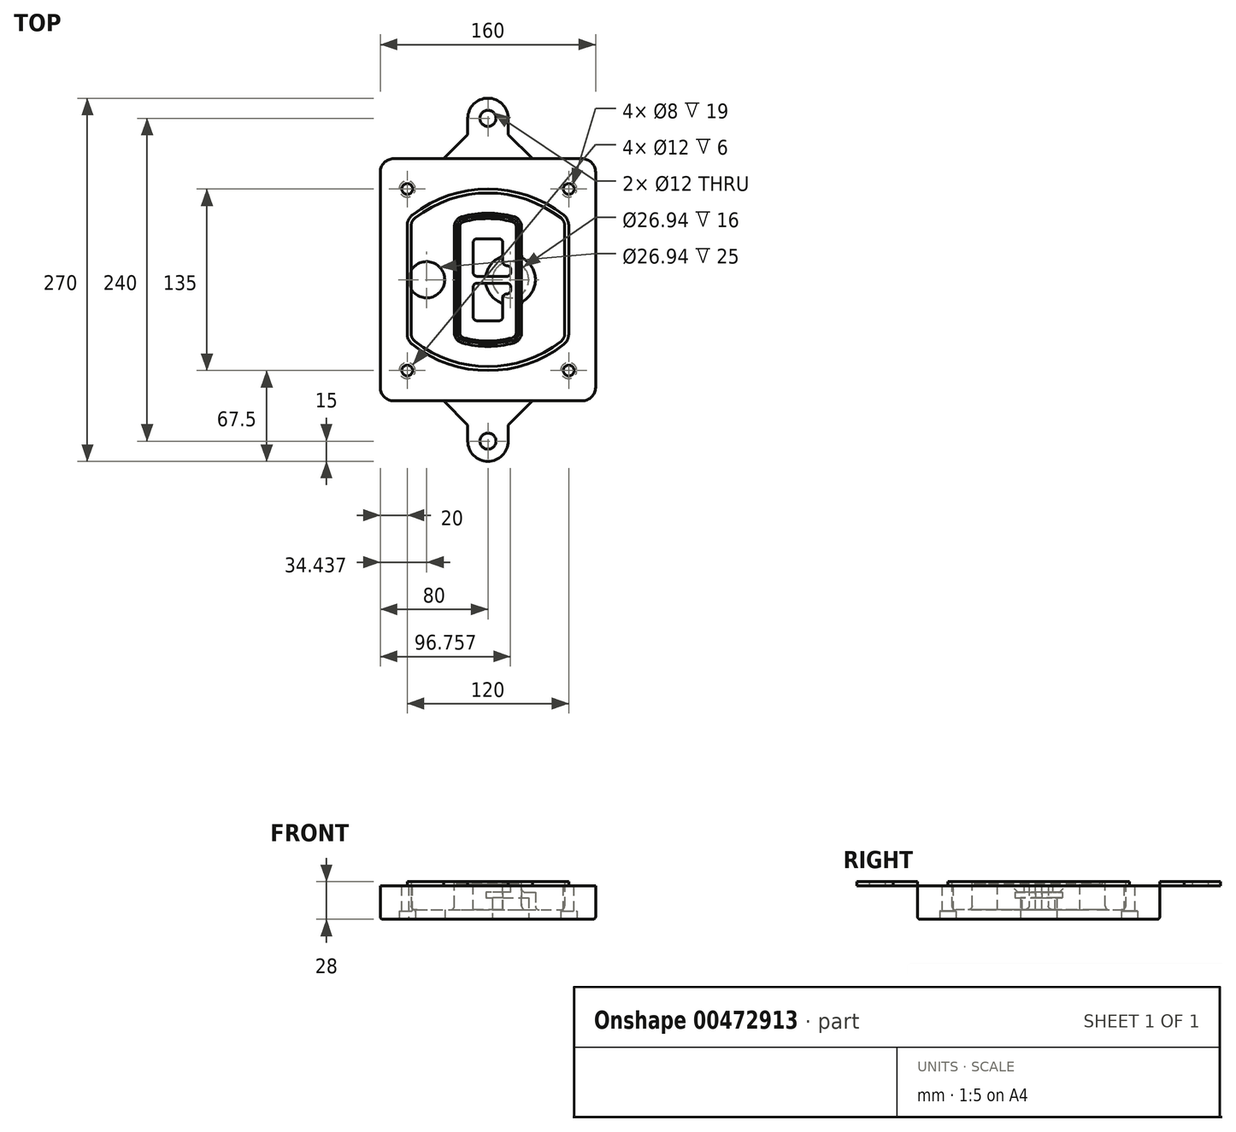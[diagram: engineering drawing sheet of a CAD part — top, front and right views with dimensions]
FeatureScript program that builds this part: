
annotation { "Feature Type Name" : "Feature", "Feature Type Description" : "" }
export const myFeature = defineFeature(function(context is Context, id is Id, definition is map)
    precondition{}
    {
        {
            var Q0;
            Q0=qCreatedBy(makeId("Top.planeOp"),FACE);
            var sketch = newSketch(context, id + "F0", { "sketchPlane" : qUnion([Q0])});
            skPoint(sketch, "E0.rect.middle", {"position": v(0, 0) * mm});
            skLineSegment(sketch, "E1.bottom", {"start": v(-70, -90) * mm, "end": v(70, -90) * mm});
            skLineSegment(sketch, "E1.top", {"start": v(-70, 90) * mm, "end": v(70, 90) * mm});
            skLineSegment(sketch, "E1.left", {"start": v(-80, -80) * mm, "end": v(-80, 80) * mm});
            skLineSegment(sketch, "E1.right", {"start": v(80, -80) * mm, "end": v(80, 80) * mm});
            skLineSegment(sketch, "E2", {"start": v(-80, 90) * mm, "end": v(80, -90) * mm, "construction": true});
            skLineSegment(sketch, "E3", {"start": v(80, 90) * mm, "end": v(-80, -90) * mm, "construction": true});
            skCircle(sketch, "E4", {"center": v(-60, 67.5) * mm, "radius": 4 * mm});
            skCircle(sketch, "E5", {"center": v(60, 67.5) * mm, "radius": 4 * mm});
            skCircle(sketch, "E6", {"center": v(60, -67.5) * mm, "radius": 4 * mm});
            skCircle(sketch, "E7", {"center": v(-60, -67.5) * mm, "radius": 4 * mm});
            skLineSegment(sketch, "E8", {"start": v(-60, 67.5) * mm, "end": v(60, 67.5) * mm, "construction": true});
            skLineSegment(sketch, "E9", {"start": v(60, 67.5) * mm, "end": v(60, -67.5) * mm, "construction": true});
            skLineSegment(sketch, "E10", {"start": v(60, -67.5) * mm, "end": v(-60, -67.5) * mm, "construction": true});
            skLineSegment(sketch, "E11", {"start": v(-60, -67.5) * mm, "end": v(-60, 67.5) * mm, "construction": true});
            skLineSegment(sketch, "E12", {"start": v(-60, 40.3) * mm, "end": v(-60, -40.3) * mm});
            skLineSegment(sketch, "E13", {"start": v(60, 40.3) * mm, "end": v(60, -40.3) * mm});
            skArc(sketch, "E14", {"start": v(56.15, 48.18) * mm, "mid": v(0, 67.5) * mm, "end": v(-56.15, 48.18) * mm});
            skArc(sketch, "E15", {"start": v(-56.15, -48.18) * mm, "mid": v(0, -67.5) * mm, "end": v(56.15, -48.18) * mm});
            skLineSegment(sketch, "E16", {"start": v(-60, 0) * mm, "end": v(60, 0) * mm, "construction": true});
            skPoint(sketch, "E17.visualSharp", {"position": v(-60, -45) * mm});
            skArc(sketch, "E17.filletArc", {"start": v(-60, -40.3) * mm, "mid": v(-58.99, -44.68) * mm, "end": v(-56.15, -48.18) * mm});
            skPoint(sketch, "E18.visualSharp", {"position": v(-60, 45) * mm});
            skArc(sketch, "E18.filletArc", {"start": v(-56.15, 48.18) * mm, "mid": v(-58.99, 44.68) * mm, "end": v(-60, 40.3) * mm});
            skPoint(sketch, "E19.visualSharp", {"position": v(60, 45) * mm});
            skArc(sketch, "E19.filletArc", {"start": v(60, 40.3) * mm, "mid": v(58.99, 44.68) * mm, "end": v(56.15, 48.18) * mm});
            skPoint(sketch, "E20.visualSharp", {"position": v(60, -45) * mm});
            skArc(sketch, "E20.filletArc", {"start": v(56.15, -48.18) * mm, "mid": v(58.99, -44.68) * mm, "end": v(60, -40.3) * mm});
            skPoint(sketch, "E21.visualSharp", {"position": v(-80, 90) * mm});
            skArc(sketch, "E21.filletArc", {"start": v(-70, 90) * mm, "mid": v(-77.07, 87.07) * mm, "end": v(-80, 80) * mm});
            skPoint(sketch, "E22.visualSharp", {"position": v(80, 90) * mm});
            skArc(sketch, "E22.filletArc", {"start": v(80, 80) * mm, "mid": v(77.07, 87.07) * mm, "end": v(70, 90) * mm});
            skPoint(sketch, "E23.visualSharp", {"position": v(80, -90) * mm});
            skArc(sketch, "E23.filletArc", {"start": v(70, -90) * mm, "mid": v(77.07, -87.07) * mm, "end": v(80, -80) * mm});
            skPoint(sketch, "E24.visualSharp", {"position": v(-80, -90) * mm});
            skArc(sketch, "E24.filletArc", {"start": v(-80, -80) * mm, "mid": v(-77.07, -87.07) * mm, "end": v(-70, -90) * mm});
            skArc(sketch, "E25.0", {"start": v(57, 40.3) * mm, "mid": v(56.3, 43.36) * mm, "end": v(54.3, 45.81) * mm});
            skLineSegment(sketch, "E25.1", {"start": v(57, 40.3) * mm, "end": v(57, -40.3) * mm});
            skArc(sketch, "E25.2", {"start": v(54.3, -45.81) * mm, "mid": v(56.3, -43.36) * mm, "end": v(57, -40.3) * mm});
            skArc(sketch, "E25.3", {"start": v(-54.3, -45.81) * mm, "mid": v(0, -64.5) * mm, "end": v(54.3, -45.81) * mm});
            skArc(sketch, "E25.4", {"start": v(-57, -40.3) * mm, "mid": v(-56.3, -43.36) * mm, "end": v(-54.3, -45.81) * mm});
            skArc(sketch, "E25.5", {"start": v(54.3, 45.81) * mm, "mid": v(0, 64.5) * mm, "end": v(-54.3, 45.81) * mm});
            skLineSegment(sketch, "E25.6", {"start": v(-57, 40.3) * mm, "end": v(-57, -40.3) * mm});
            skArc(sketch, "E25.7", {"start": v(-54.3, 45.81) * mm, "mid": v(-56.3, 43.36) * mm, "end": v(-57, 40.3) * mm});
            skArc(sketch, "E26.0", {"start": v(-58.62, 51.33) * mm, "mid": v(-62.58, 46.43) * mm, "end": v(-64, 40.3) * mm});
            skArc(sketch, "E26.1", {"start": v(58.62, 51.33) * mm, "mid": v(0, 71.5) * mm, "end": v(-58.62, 51.33) * mm});
            skArc(sketch, "E26.2", {"start": v(64, 40.3) * mm, "mid": v(62.58, 46.43) * mm, "end": v(58.62, 51.33) * mm});
            skLineSegment(sketch, "E26.3", {"start": v(64, 40.3) * mm, "end": v(64, -40.3) * mm});
            skArc(sketch, "E26.4", {"start": v(58.62, -51.33) * mm, "mid": v(62.58, -46.43) * mm, "end": v(64, -40.3) * mm});
            skLineSegment(sketch, "E26.5", {"start": v(-64, 40.3) * mm, "end": v(-64, -40.3) * mm});
            skArc(sketch, "E26.6", {"start": v(-58.62, -51.33) * mm, "mid": v(0, -71.5) * mm, "end": v(58.62, -51.33) * mm});
            skArc(sketch, "E26.7", {"start": v(-64, -40.3) * mm, "mid": v(-62.58, -46.43) * mm, "end": v(-58.62, -51.33) * mm});
            skSolve(sketch);
        }
        {
            var Q0;
            Q0=makeQuery(id+"F0.imprint","IMPRINT",FACE,{"disambiguationData":[TD([[makeQuery(id+"F0.imprint","IMPRINT",EDGE,{"derivedFrom":sQuery(id+"F0.wireOp",EDGE,"E1.bottom")}),1.0]])]});
            var Q1;
            Q1=makeQuery(id+"F0.imprint","IMPRINT",FACE,{"disambiguationData":[TD([[makeQuery(id+"F0.imprint","IMPRINT",EDGE,{"derivedFrom":sQuery(id+"F0.wireOp",EDGE,"E12")}),1.0]])]});
            var Q2;
            Q2=makeQuery(id+"F0.imprint","IMPRINT",FACE,{"disambiguationData":[TD([[makeQuery(id+"F0.imprint","IMPRINT",EDGE,{"derivedFrom":sQuery(id+"F0.wireOp",EDGE,"E25.0")}),1.0]])]});
            var Q3;
            Q3=makeQuery(id+"F0.imprint","IMPRINT",FACE,{"disambiguationData":[TD([[makeQuery(id+"F0.imprint","IMPRINT",EDGE,{"derivedFrom":sQuery(id+"F0.wireOp",EDGE,"E12")}),-1.0]])]});
            extrude(context, id + "F1", {"entities" : qUnion([Q0, Q1, Q2, Q3]), "oppositeDirection" : true, "depth" : 25 * mm});
        }
        {
            var Q0;
            Q0=makeQuery(id+"F0.imprint","IMPRINT",FACE,{"disambiguationData":[TD([[makeQuery(id+"F0.imprint","IMPRINT",EDGE,{"derivedFrom":sQuery(id+"F0.wireOp",EDGE,"E12")}),1.0]])]});
            extrude(context, id + "F2", {"entities" : qUnion([Q0]), "operationType" : NewBodyOperationType.ADD, "depth" : 3 * mm});
        }
        {
            var Q0;
            Q0=makeQuery(id+"F0.imprint","IMPRINT",FACE,{"disambiguationData":[TD([[makeQuery(id+"F0.imprint","IMPRINT",EDGE,{"derivedFrom":sQuery(id+"F0.wireOp",EDGE,"E25.0")}),1.0]])]});
            extrude(context, id + "F3", {"entities" : qUnion([Q0]), "operationType" : NewBodyOperationType.REMOVE, "oppositeDirection" : true, "depth" : 18 * mm});
        }
        {
            var Q0;
            Q0=makeQuery(id+"F2.opExtrude","CAP_FACE",FACE,{"disambiguationData":[OSD([sQuery(id+"F0.wireOp",EDGE,"E12"),sQuery(id+"F0.wireOp",EDGE,"E13"),sQuery(id+"F0.wireOp",EDGE,"E14"),sQuery(id+"F0.wireOp",EDGE,"E15"),sQuery(id+"F0.wireOp",EDGE,"E17.filletArc"),sQuery(id+"F0.wireOp",EDGE,"E18.filletArc"),sQuery(id+"F0.wireOp",EDGE,"E19.filletArc"),sQuery(id+"F0.wireOp",EDGE,"E20.filletArc"),sQuery(id+"F0.wireOp",EDGE,"E25.0"),sQuery(id+"F0.wireOp",EDGE,"E25.1"),sQuery(id+"F0.wireOp",EDGE,"E25.2"),sQuery(id+"F0.wireOp",EDGE,"E25.3"),sQuery(id+"F0.wireOp",EDGE,"E25.4"),sQuery(id+"F0.wireOp",EDGE,"E25.5"),sQuery(id+"F0.wireOp",EDGE,"E25.6"),sQuery(id+"F0.wireOp",EDGE,"E25.7")])],"isStart":false});
            var sketch = newSketch(context, id + "F4", { "sketchPlane" : qUnion([Q0])});
            skArc(sketch, "E27.0", {"start": v(-19.08, -46.97) * mm, "mid": v(0, -49.5) * mm, "end": v(19.08, -46.97) * mm});
            skArc(sketch, "E28.0", {"start": v(19.08, 46.97) * mm, "mid": v(0, 49.5) * mm, "end": v(-19.08, 46.97) * mm});
            skLineSegment(sketch, "E29", {"start": v(-25, 39.25) * mm, "end": v(-25, -39.25) * mm});
            skLineSegment(sketch, "E30", {"start": v(25, 39.25) * mm, "end": v(25, -39.25) * mm});
            skLineSegment(sketch, "E31", {"start": v(-25, 45.1) * mm, "end": v(25, 45.1) * mm, "construction": true});
            skLineSegment(sketch, "E32", {"start": v(-25, -45.1) * mm, "end": v(25, -45.1) * mm, "construction": true});
            skPoint(sketch, "E33.visualSharp", {"position": v(-25, 45.1) * mm});
            skArc(sketch, "E33.filletArc", {"start": v(-19.08, 46.97) * mm, "mid": v(-23.35, 44.11) * mm, "end": v(-25, 39.25) * mm});
            skPoint(sketch, "E34.visualSharp", {"position": v(25, 45.1) * mm});
            skArc(sketch, "E34.filletArc", {"start": v(25, 39.25) * mm, "mid": v(23.35, 44.11) * mm, "end": v(19.08, 46.97) * mm});
            skPoint(sketch, "E35.visualSharp", {"position": v(25, -45.1) * mm});
            skArc(sketch, "E35.filletArc", {"start": v(19.08, -46.97) * mm, "mid": v(23.35, -44.11) * mm, "end": v(25, -39.25) * mm});
            skPoint(sketch, "E36.visualSharp", {"position": v(-25, -45.1) * mm});
            skArc(sketch, "E36.filletArc", {"start": v(-25, -39.25) * mm, "mid": v(-23.35, -44.11) * mm, "end": v(-19.08, -46.97) * mm});
            skArc(sketch, "E37.0", {"start": v(54.3, 45.81) * mm, "mid": v(0, 64.5) * mm, "end": v(-54.3, 45.81) * mm});
            skArc(sketch, "E37.1", {"start": v(-54.3, 45.81) * mm, "mid": v(-56.3, 43.36) * mm, "end": v(-57, 40.3) * mm});
            skLineSegment(sketch, "E37.2", {"start": v(-57, 40.3) * mm, "end": v(-57, -40.3) * mm});
            skArc(sketch, "E37.3", {"start": v(-57, -40.3) * mm, "mid": v(-56.3, -43.36) * mm, "end": v(-54.3, -45.81) * mm});
            skArc(sketch, "E37.4", {"start": v(-54.3, -45.81) * mm, "mid": v(0, -64.5) * mm, "end": v(54.3, -45.81) * mm});
            skArc(sketch, "E37.5", {"start": v(54.3, -45.81) * mm, "mid": v(56.3, -43.36) * mm, "end": v(57, -40.3) * mm});
            skLineSegment(sketch, "E37.6", {"start": v(57, 40.3) * mm, "end": v(57, -40.3) * mm});
            skArc(sketch, "E37.7", {"start": v(57, 40.3) * mm, "mid": v(56.3, 43.36) * mm, "end": v(54.3, 45.81) * mm});
            skLineSegment(sketch, "E38.0", {"start": v(23, 39.25) * mm, "end": v(23, -39.25) * mm});
            skArc(sketch, "E38.1", {"start": v(18.56, -45.04) * mm, "mid": v(21.76, -42.9) * mm, "end": v(23, -39.25) * mm});
            skArc(sketch, "E38.2", {"start": v(-18.56, -45.04) * mm, "mid": v(0, -47.5) * mm, "end": v(18.56, -45.04) * mm});
            skArc(sketch, "E38.3", {"start": v(-23, -39.25) * mm, "mid": v(-21.76, -42.9) * mm, "end": v(-18.56, -45.04) * mm});
            skLineSegment(sketch, "E38.4", {"start": v(-23, 39.25) * mm, "end": v(-23, -39.25) * mm});
            skArc(sketch, "E38.5", {"start": v(23, 39.25) * mm, "mid": v(21.76, 42.9) * mm, "end": v(18.56, 45.04) * mm});
            skArc(sketch, "E38.6", {"start": v(-18.56, 45.04) * mm, "mid": v(-21.76, 42.9) * mm, "end": v(-23, 39.25) * mm});
            skArc(sketch, "E38.7", {"start": v(18.56, 45.04) * mm, "mid": v(0, 47.5) * mm, "end": v(-18.56, 45.04) * mm});
            skArc(sketch, "E39.0", {"start": v(21, 39.25) * mm, "mid": v(20.18, 41.68) * mm, "end": v(18.04, 43.1) * mm});
            skLineSegment(sketch, "E39.1", {"start": v(21, 39.25) * mm, "end": v(21, -39.25) * mm});
            skArc(sketch, "E39.2", {"start": v(18.04, -43.1) * mm, "mid": v(20.18, -41.68) * mm, "end": v(21, -39.25) * mm});
            skArc(sketch, "E39.3", {"start": v(-18.04, -43.1) * mm, "mid": v(0, -45.5) * mm, "end": v(18.04, -43.1) * mm});
            skArc(sketch, "E39.4", {"start": v(-21, -39.25) * mm, "mid": v(-20.18, -41.68) * mm, "end": v(-18.04, -43.1) * mm});
            skArc(sketch, "E39.5", {"start": v(18.04, 43.1) * mm, "mid": v(0, 45.5) * mm, "end": v(-18.04, 43.1) * mm});
            skLineSegment(sketch, "E39.6", {"start": v(-21, 39.25) * mm, "end": v(-21, -39.25) * mm});
            skArc(sketch, "E39.7", {"start": v(-18.04, 43.1) * mm, "mid": v(-20.18, 41.68) * mm, "end": v(-21, 39.25) * mm});
            skLineSegment(sketch, "E40", {"start": v(-25, 0) * mm, "end": v(25, 0) * mm, "construction": true});
            skLineSegment(sketch, "E41", {"start": v(-11, 5.5) * mm, "end": v(-11, 27.5) * mm});
            skLineSegment(sketch, "E42", {"start": v(-8, 30.5) * mm, "end": v(8, 30.5) * mm});
            skLineSegment(sketch, "E43", {"start": v(11, 27.5) * mm, "end": v(11, 13.5) * mm});
            skLineSegment(sketch, "E44", {"start": v(14, 10.5) * mm, "end": v(14, 10.5) * mm});
            skLineSegment(sketch, "E45", {"start": v(17, 7.5) * mm, "end": v(17, 5.5) * mm});
            skLineSegment(sketch, "E46", {"start": v(14, 2.5) * mm, "end": v(-8, 2.5) * mm});
            skPoint(sketch, "E47.visualSharp", {"position": v(-11, 30.5) * mm});
            skArc(sketch, "E47.filletArc", {"start": v(-8, 30.5) * mm, "mid": v(-10.12, 29.62) * mm, "end": v(-11, 27.5) * mm});
            skPoint(sketch, "E48.visualSharp", {"position": v(11, 30.5) * mm});
            skArc(sketch, "E48.filletArc", {"start": v(11, 27.5) * mm, "mid": v(10.12, 29.62) * mm, "end": v(8, 30.5) * mm});
            skPoint(sketch, "E49.visualSharp", {"position": v(11, 10.5) * mm});
            skArc(sketch, "E49.filletArc", {"start": v(11, 13.5) * mm, "mid": v(11.88, 11.38) * mm, "end": v(14, 10.5) * mm});
            skPoint(sketch, "E50.visualSharp", {"position": v(17, 10.5) * mm});
            skArc(sketch, "E50.filletArc", {"start": v(17, 7.5) * mm, "mid": v(16.12, 9.62) * mm, "end": v(14, 10.5) * mm});
            skPoint(sketch, "E51.visualSharp", {"position": v(17, 2.5) * mm});
            skArc(sketch, "E51.filletArc", {"start": v(14, 2.5) * mm, "mid": v(16.12, 3.38) * mm, "end": v(17, 5.5) * mm});
            skPoint(sketch, "E52.visualSharp", {"position": v(-11, 2.5) * mm});
            skArc(sketch, "E52.filletArc", {"start": v(-11, 5.5) * mm, "mid": v(-10.12, 3.38) * mm, "end": v(-8, 2.5) * mm});
            skLineSegment(sketch, "E53.0.MirrorCS", {"start": v(14, -2.5) * mm, "end": v(-8, -2.5) * mm});
            skArc(sketch, "E54.0.MirrorCS", {"start": v(-11, -5.5) * mm, "mid": v(-10.12, -3.38) * mm, "end": v(-8, -2.5) * mm});
            skLineSegment(sketch, "E55.0.MirrorCS", {"start": v(-11, -5.5) * mm, "end": v(-11, -27.5) * mm});
            skArc(sketch, "E56.0.MirrorCS", {"start": v(-8, -30.5) * mm, "mid": v(-10.12, -29.62) * mm, "end": v(-11, -27.5) * mm});
            skLineSegment(sketch, "E57.0.MirrorCS", {"start": v(-8, -30.5) * mm, "end": v(8, -30.5) * mm});
            skArc(sketch, "E58.0.MirrorCS", {"start": v(11, -27.5) * mm, "mid": v(10.12, -29.62) * mm, "end": v(8, -30.5) * mm});
            skLineSegment(sketch, "E59.0.MirrorCS", {"start": v(11, -27.5) * mm, "end": v(11, -13.5) * mm});
            skArc(sketch, "E60.0.MirrorCS", {"start": v(11, -13.5) * mm, "mid": v(11.88, -11.38) * mm, "end": v(14, -10.5) * mm});
            skArc(sketch, "E61.0.MirrorCS", {"start": v(17, -7.5) * mm, "mid": v(16.12, -9.62) * mm, "end": v(14, -10.5) * mm});
            skLineSegment(sketch, "E62.0.MirrorCS", {"start": v(17, -7.5) * mm, "end": v(17, -5.5) * mm});
            skArc(sketch, "E63.0.MirrorCS", {"start": v(14, -2.5) * mm, "mid": v(16.12, -3.38) * mm, "end": v(17, -5.5) * mm});
            skSolve(sketch);
        }
        {
            var Q0;
            Q0=makeQuery(id+"F4.imprint","IMPRINT",FACE,{"disambiguationData":[TD([[makeQuery(id+"F4.imprint","IMPRINT",EDGE,{"derivedFrom":sQuery(id+"F4.wireOp",EDGE,"E27.0")}),1.0]])]});
            var Q1;
            Q1=makeQuery(id+"F4.imprint","IMPRINT",FACE,{"disambiguationData":[TD([[makeQuery(id+"F4.imprint","IMPRINT",EDGE,{"derivedFrom":sQuery(id+"F4.wireOp",EDGE,"E38.0")}),-1.0]])]});
            var Q2;
            Q2=makeQuery(id+"F4.imprint","IMPRINT",FACE,{"disambiguationData":[TD([[makeQuery(id+"F4.imprint","IMPRINT",EDGE,{"derivedFrom":sQuery(id+"F4.wireOp",EDGE,"E39.0")}),1.0]])]});
            extrude(context, id + "F5", {"entities" : qUnion([Q0, Q1, Q2]), "operationType" : NewBodyOperationType.ADD, "endBound" : BoundingType.UP_TO_NEXT, "oppositeDirection" : true, "depth" : 25 * mm});
        }
        {
            var Q0;
            Q0=makeQuery(id+"F4.imprint","IMPRINT",FACE,{"disambiguationData":[TD([[makeQuery(id+"F4.imprint","IMPRINT",EDGE,{"derivedFrom":sQuery(id+"F4.wireOp",EDGE,"E38.0")}),-1.0]])]});
            extrude(context, id + "F6", {"entities" : qUnion([Q0]), "operationType" : NewBodyOperationType.REMOVE, "oppositeDirection" : true, "depth" : 2 * mm});
        }
        {
            var Q0;
            Q0=makeQuery(id+"F1.opExtrude","CAP_FACE",FACE,{"disambiguationData":[OSD([sQuery(id+"F0.wireOp",EDGE,"E1.bottom"),sQuery(id+"F0.wireOp",EDGE,"E1.top"),sQuery(id+"F0.wireOp",EDGE,"E1.left"),sQuery(id+"F0.wireOp",EDGE,"E1.right"),sQuery(id+"F0.wireOp",EDGE,"E4"),sQuery(id+"F0.wireOp",EDGE,"E5"),sQuery(id+"F0.wireOp",EDGE,"E6"),sQuery(id+"F0.wireOp",EDGE,"E7"),sQuery(id+"F0.wireOp",EDGE,"E21.filletArc"),sQuery(id+"F0.wireOp",EDGE,"E22.filletArc"),sQuery(id+"F0.wireOp",EDGE,"E23.filletArc"),sQuery(id+"F0.wireOp",EDGE,"E24.filletArc")])],"isStart":false});
            var sketch = newSketch(context, id + "F7", { "sketchPlane" : qUnion([Q0])});
            skCircle(sketch, "E64", {"center": v(16.76, 0) * mm, "radius": 13.47 * mm});
            skCircle(sketch, "E65", {"center": v(-45.56, 0) * mm, "radius": 13.47 * mm});
            skLineSegment(sketch, "E66", {"start": v(80, 0) * mm, "end": v(-80, 0) * mm});
            skCircle(sketch, "E67", {"center": v(16.76, 0) * mm, "radius": 18.47 * mm});
            skCircle(sketch, "E68", {"center": v(60, -67.5) * mm, "radius": 6 * mm});
            skCircle(sketch, "E69", {"center": v(-60, -67.5) * mm, "radius": 6 * mm});
            skCircle(sketch, "E70", {"center": v(-60, 67.5) * mm, "radius": 6 * mm});
            skCircle(sketch, "E71", {"center": v(60, 67.5) * mm, "radius": 6 * mm});
            skSolve(sketch);
        }
        {
            var Q0;
            {var subQ1=sQuery(id+"F7.wireOp",EDGE,"E66");var subQ4=sQuery(id+"F7.wireOp",EDGE,"E64");var subQ6=makeQuery(id+"F7.imprint","INTERSECT",VERTEX,{"disambiguationData":[OD(0.0)],"derivedFrom":[subQ4,subQ1]});Q0=makeQuery(id+"F7.imprint","IMPRINT",FACE,{"disambiguationData":[TD([[makeQuery(id+"F7.imprint","IMPRINT",EDGE,{"disambiguationData":[TD([[subQ6,-1.0]])],"derivedFrom":subQ4}),-1.0]])]});}
            var Q1;
            {var subQ0=sQuery(id+"F7.wireOp",EDGE,"E66");var subQ1=sQuery(id+"F7.wireOp",EDGE,"E64");var subQ3=makeQuery(id+"F7.imprint","INTERSECT",VERTEX,{"disambiguationData":[OD(0.0)],"derivedFrom":[subQ1,subQ0]});Q1=makeQuery(id+"F7.imprint","IMPRINT",FACE,{"disambiguationData":[TD([[makeQuery(id+"F7.imprint","IMPRINT",EDGE,{"disambiguationData":[TD([[subQ3,-1.0]])],"derivedFrom":subQ1}),1.0]])]});}
            var Q2;
            {var subQ0=sQuery(id+"F7.wireOp",EDGE,"E66");var subQ1=sQuery(id+"F7.wireOp",EDGE,"E64");var subQ3=makeQuery(id+"F7.imprint","INTERSECT",VERTEX,{"disambiguationData":[OD(0.0)],"derivedFrom":[subQ1,subQ0]});Q2=makeQuery(id+"F7.imprint","IMPRINT",FACE,{"disambiguationData":[TD([[makeQuery(id+"F7.imprint","IMPRINT",EDGE,{"disambiguationData":[TD([[subQ3,1.0]])],"derivedFrom":subQ1}),1.0]])]});}
            var Q3;
            {var subQ1=sQuery(id+"F7.wireOp",EDGE,"E66");var subQ4=sQuery(id+"F7.wireOp",EDGE,"E64");var subQ6=makeQuery(id+"F7.imprint","INTERSECT",VERTEX,{"disambiguationData":[OD(0.0)],"derivedFrom":[subQ4,subQ1]});Q3=makeQuery(id+"F7.imprint","IMPRINT",FACE,{"disambiguationData":[TD([[makeQuery(id+"F7.imprint","IMPRINT",EDGE,{"disambiguationData":[TD([[subQ6,1.0]])],"derivedFrom":subQ4}),-1.0]])]});}
            extrude(context, id + "F8", {"entities" : qUnion([Q0, Q1, Q2, Q3]), "operationType" : NewBodyOperationType.ADD, "oppositeDirection" : true, "depth" : 20 * mm});
        }
        {
            var Q0;
            {var subQ0=sQuery(id+"F7.wireOp",EDGE,"E66");var subQ1=sQuery(id+"F7.wireOp",EDGE,"E64");var subQ3=makeQuery(id+"F7.imprint","INTERSECT",VERTEX,{"disambiguationData":[OD(0.0)],"derivedFrom":[subQ1,subQ0]});Q0=makeQuery(id+"F7.imprint","IMPRINT",FACE,{"disambiguationData":[TD([[makeQuery(id+"F7.imprint","IMPRINT",EDGE,{"disambiguationData":[TD([[subQ3,-1.0]])],"derivedFrom":subQ1}),1.0]])]});}
            var Q1;
            {var subQ0=sQuery(id+"F7.wireOp",EDGE,"E66");var subQ1=sQuery(id+"F7.wireOp",EDGE,"E64");var subQ3=makeQuery(id+"F7.imprint","INTERSECT",VERTEX,{"disambiguationData":[OD(0.0)],"derivedFrom":[subQ1,subQ0]});Q1=makeQuery(id+"F7.imprint","IMPRINT",FACE,{"disambiguationData":[TD([[makeQuery(id+"F7.imprint","IMPRINT",EDGE,{"disambiguationData":[TD([[subQ3,1.0]])],"derivedFrom":subQ1}),1.0]])]});}
            extrude(context, id + "F9", {"entities" : qUnion([Q0, Q1]), "operationType" : NewBodyOperationType.REMOVE, "oppositeDirection" : true, "depth" : 16 * mm});
        }
        {
            var Q0;
            {var subQ0=sQuery(id+"F7.wireOp",EDGE,"E66");var subQ1=sQuery(id+"F7.wireOp",EDGE,"E65");var subQ3=makeQuery(id+"F7.imprint","INTERSECT",VERTEX,{"disambiguationData":[OD(0.0)],"derivedFrom":[subQ1,subQ0]});Q0=makeQuery(id+"F7.imprint","IMPRINT",FACE,{"disambiguationData":[TD([[makeQuery(id+"F7.imprint","IMPRINT",EDGE,{"disambiguationData":[TD([[subQ3,-1.0]])],"derivedFrom":subQ1}),1.0]])]});}
            var Q1;
            {var subQ0=sQuery(id+"F7.wireOp",EDGE,"E66");var subQ1=sQuery(id+"F7.wireOp",EDGE,"E65");var subQ3=makeQuery(id+"F7.imprint","INTERSECT",VERTEX,{"disambiguationData":[OD(0.0)],"derivedFrom":[subQ1,subQ0]});Q1=makeQuery(id+"F7.imprint","IMPRINT",FACE,{"disambiguationData":[TD([[makeQuery(id+"F7.imprint","IMPRINT",EDGE,{"disambiguationData":[TD([[subQ3,1.0]])],"derivedFrom":subQ1}),1.0]])]});}
            extrude(context, id + "F10", {"entities" : qUnion([Q0, Q1]), "operationType" : NewBodyOperationType.REMOVE, "oppositeDirection" : true, "depth" : 25 * mm});
        }
        {
            var Q0;
            Q0=makeQuery(id+"F7.imprint","IMPRINT",FACE,{"disambiguationData":[TD([[makeQuery(id+"F7.imprint","IMPRINT",EDGE,{"derivedFrom":sQuery(id+"F7.wireOp",EDGE,"E68")}),1.0]])]});
            var Q1;
            Q1=makeQuery(id+"F7.imprint","IMPRINT",FACE,{"disambiguationData":[TD([[makeQuery(id+"F7.imprint","IMPRINT",EDGE,{"derivedFrom":makeQuery(id+"F1.opExtrude","CAP_EDGE",EDGE,{"disambiguationData":[OSD([sQuery(id+"F0.wireOp",EDGE,"E5")])],"isStart":false})}),-1.0]])]});
            var Q2;
            Q2=makeQuery(id+"F7.imprint","IMPRINT",FACE,{"disambiguationData":[TD([[makeQuery(id+"F7.imprint","IMPRINT",EDGE,{"derivedFrom":sQuery(id+"F7.wireOp",EDGE,"E69")}),1.0]])]});
            var Q3;
            Q3=makeQuery(id+"F7.imprint","IMPRINT",FACE,{"disambiguationData":[TD([[makeQuery(id+"F7.imprint","IMPRINT",EDGE,{"derivedFrom":makeQuery(id+"F1.opExtrude","CAP_EDGE",EDGE,{"disambiguationData":[OSD([sQuery(id+"F0.wireOp",EDGE,"E4")])],"isStart":false})}),-1.0]])]});
            var Q4;
            Q4=makeQuery(id+"F7.imprint","IMPRINT",FACE,{"disambiguationData":[TD([[makeQuery(id+"F7.imprint","IMPRINT",EDGE,{"derivedFrom":sQuery(id+"F7.wireOp",EDGE,"E70")}),1.0]])]});
            var Q5;
            Q5=makeQuery(id+"F7.imprint","IMPRINT",FACE,{"disambiguationData":[TD([[makeQuery(id+"F7.imprint","IMPRINT",EDGE,{"derivedFrom":makeQuery(id+"F1.opExtrude","CAP_EDGE",EDGE,{"disambiguationData":[OSD([sQuery(id+"F0.wireOp",EDGE,"E7")])],"isStart":false})}),-1.0]])]});
            var Q6;
            Q6=makeQuery(id+"F7.imprint","IMPRINT",FACE,{"disambiguationData":[TD([[makeQuery(id+"F7.imprint","IMPRINT",EDGE,{"derivedFrom":sQuery(id+"F7.wireOp",EDGE,"E71")}),1.0]])]});
            var Q7;
            Q7=makeQuery(id+"F7.imprint","IMPRINT",FACE,{"disambiguationData":[TD([[makeQuery(id+"F7.imprint","IMPRINT",EDGE,{"derivedFrom":makeQuery(id+"F1.opExtrude","CAP_EDGE",EDGE,{"disambiguationData":[OSD([sQuery(id+"F0.wireOp",EDGE,"E6")])],"isStart":false})}),-1.0]])]});
            extrude(context, id + "F11", {"entities" : qUnion([Q0, Q1, Q2, Q3, Q4, Q5, Q6, Q7]), "operationType" : NewBodyOperationType.REMOVE, "oppositeDirection" : true, "depth" : 6 * mm});
        }
        {
            var Q0;
            Q0=makeQuery(id+"F9.boolean.opBoolean","COPY",FACE,{"derivedFrom":makeQuery(id+"F9.opExtrude","CAP_FACE",FACE,{"disambiguationData":[OSD([sQuery(id+"F7.wireOp",EDGE,"E64")])],"isStart":false})});
            var sketch = newSketch(context, id + "F12", { "sketchPlane" : qUnion([Q0])});
            skArc(sketch, "E72.0", {"start": v(11, 17.55) * mm, "mid": v(2.57, 11.82) * mm, "end": v(-1.54, 2.5) * mm});
            skArc(sketch, "E72.1", {"start": v(-1.54, -2.5) * mm, "mid": v(2.57, -11.82) * mm, "end": v(11, -17.55) * mm});
            skLineSegment(sketch, "E73", {"start": v(-1.54, -2.5) * mm, "end": v(14, -2.5) * mm});
            skLineSegment(sketch, "E74.0", {"start": v(14, 2.5) * mm, "end": v(-1.54, 2.5) * mm});
            skArc(sketch, "E74.1", {"start": v(14, 2.5) * mm, "mid": v(16.12, 3.38) * mm, "end": v(17, 5.5) * mm});
            skLineSegment(sketch, "E74.2", {"start": v(17, 7.5) * mm, "end": v(17, 5.5) * mm});
            skArc(sketch, "E74.3", {"start": v(17, 7.5) * mm, "mid": v(16.12, 9.62) * mm, "end": v(14, 10.5) * mm});
            skArc(sketch, "E74.4", {"start": v(11, 13.5) * mm, "mid": v(11.88, 11.38) * mm, "end": v(14, 10.5) * mm});
            skLineSegment(sketch, "E74.5", {"start": v(11, 17.55) * mm, "end": v(11, 13.5) * mm});
            skLineSegment(sketch, "E74.7", {"start": v(14, -2.5) * mm, "end": v(-1.54, -2.5) * mm});
            skArc(sketch, "E74.8", {"start": v(14, -2.5) * mm, "mid": v(16.12, -3.38) * mm, "end": v(17, -5.5) * mm});
            skLineSegment(sketch, "E74.9", {"start": v(17, -7.5) * mm, "end": v(17, -5.5) * mm});
            skArc(sketch, "E74.10", {"start": v(17, -7.5) * mm, "mid": v(16.12, -9.62) * mm, "end": v(14, -10.5) * mm});
            skArc(sketch, "E74.11", {"start": v(11, -13.5) * mm, "mid": v(11.88, -11.38) * mm, "end": v(14, -10.5) * mm});
            skLineSegment(sketch, "E74.12", {"start": v(11, -17.55) * mm, "end": v(11, -13.5) * mm});
            skPoint(sketch, "E75.orphan", {"position": v(11, -27.5) * mm});
            skPoint(sketch, "E76.orphan", {"position": v(-8, -2.5) * mm});
            skPoint(sketch, "E77.orphan", {"position": v(-8, 2.5) * mm});
            skPoint(sketch, "E78.orphan", {"position": v(11, 27.5) * mm});
            skSolve(sketch);
        }
        {
            var Q0;
            {var subQ7=sQuery(id+"F12.wireOp",EDGE,"E72.0");var subQ14=sQuery(id+"F12.wireOp",EDGE,"E72.1");var subQ16=sQuery(id+"F12.wireOp",EDGE,"E74.1");var subQ18=sQuery(id+"F12.wireOp",EDGE,"E74.8");Q0=qUnion([makeQuery(id+"F12.imprint","IMPRINT",FACE,{"disambiguationData":[TD([[makeQuery(id+"F12.imprint","IMPRINT",EDGE,{"derivedFrom":subQ7}),1.0]])]}),makeQuery(id+"F12.imprint","IMPRINT",FACE,{"disambiguationData":[TD([[makeQuery(id+"F12.imprint","IMPRINT",EDGE,{"derivedFrom":subQ14}),1.0]])]}),makeQuery(id+"F12.imprint","IMPRINT",FACE,{"disambiguationData":[TD([[makeQuery(id+"F12.imprint","IMPRINT",EDGE,{"derivedFrom":subQ16}),1.0]])]}),makeQuery(id+"F12.imprint","IMPRINT",FACE,{"disambiguationData":[TD([[makeQuery(id+"F12.imprint","IMPRINT",EDGE,{"derivedFrom":subQ18}),-1.0]])]})]);}
            var Q1;
            Q1=makeQuery(id+"F5.boolean.opBoolean","SPLIT",FACE,{"disambiguationData":[TD([makeQuery(id+"F5.opExtrude","SWEPT_FACE",FACE,{"disambiguationData":[OSD([sQuery(id+"F4.wireOp",EDGE,"E41")])]})])],"derivedFrom":makeQuery(id+"F3.boolean.opBoolean","COPY",FACE,{"derivedFrom":makeQuery(id+"F3.opExtrude","CAP_FACE",FACE,{"disambiguationData":[OSD([sQuery(id+"F0.wireOp",EDGE,"E25.0"),sQuery(id+"F0.wireOp",EDGE,"E25.1"),sQuery(id+"F0.wireOp",EDGE,"E25.2"),sQuery(id+"F0.wireOp",EDGE,"E25.3"),sQuery(id+"F0.wireOp",EDGE,"E25.4"),sQuery(id+"F0.wireOp",EDGE,"E25.5"),sQuery(id+"F0.wireOp",EDGE,"E25.6"),sQuery(id+"F0.wireOp",EDGE,"E25.7")])],"isStart":false})})});
            extrude(context, id + "F13", {"entities" : qUnion([Q0]), "operationType" : NewBodyOperationType.REMOVE, "endBound" : BoundingType.UP_TO_SURFACE, "endBoundEntityFace" : qUnion([Q1]), "depth" : 25 * mm});
        }
        {
            var Q0;
            Q0=makeQuery(id+"F3.boolean.opBoolean","COPY",EDGE,{"derivedFrom":makeQuery(id+"F3.opExtrude","CAP_EDGE",EDGE,{"disambiguationData":[OSD([sQuery(id+"F0.wireOp",EDGE,"E25.6")])],"isStart":false})});
            var Q1;
            Q1=makeQuery(id+"F8.boolean.opBoolean","INTERSECT",EDGE,{"derivedFrom":[makeQuery(id+"F5.opExtrude","SWEPT_FACE",FACE,{"disambiguationData":[OSD([sQuery(id+"F4.wireOp",EDGE,"E30")])]}),makeQuery(id+"F8.opExtrude","CAP_FACE",FACE,{"disambiguationData":[OSD([sQuery(id+"F7.wireOp",EDGE,"E67")])],"isStart":false})]});
            var Q2;
            Q2=makeQuery(id+"F8.boolean.opBoolean","INTERSECT",EDGE,{"disambiguationData":[OD(1.0)],"derivedFrom":[makeQuery(id+"F5.opExtrude","SWEPT_FACE",FACE,{"disambiguationData":[OSD([sQuery(id+"F4.wireOp",EDGE,"E30")])]}),makeQuery(id+"F8.opExtrude","SWEPT_FACE",FACE,{"disambiguationData":[OSD([sQuery(id+"F7.wireOp",EDGE,"E67")])]})]});
            var Q3;
            {var subQ0=sQuery(id+"F4.wireOp",EDGE,"E30");Q3=makeQuery(id+"F8.boolean.opBoolean","SPLIT",EDGE,{"disambiguationData":[TD([makeQuery(id+"F5.opExtrude","SWEPT_FACE",FACE,{"disambiguationData":[OSD([sQuery(id+"F4.wireOp",EDGE,"E35.filletArc")])]})])],"derivedFrom":makeQuery(id+"F5.opExtrude","CAP_EDGE",EDGE,{"disambiguationData":[OSD([subQ0])],"isStart":false})});}
            var Q4;
            {var subQ0=sQuery(id+"F0.wireOp",EDGE,"E25.7");var subQ1=sQuery(id+"F0.wireOp",EDGE,"E25.1");var subQ2=sQuery(id+"F0.wireOp",EDGE,"E25.6");var subQ3=sQuery(id+"F0.wireOp",EDGE,"E25.5");var subQ4=sQuery(id+"F0.wireOp",EDGE,"E25.4");var subQ5=sQuery(id+"F0.wireOp",EDGE,"E25.0");var subQ6=sQuery(id+"F0.wireOp",EDGE,"E25.2");var subQ7=sQuery(id+"F0.wireOp",EDGE,"E25.3");Q4=makeQuery(id+"F8.boolean.opBoolean","INTERSECT",EDGE,{"derivedFrom":[makeQuery(id+"F5.boolean.opBoolean","SPLIT",FACE,{"disambiguationData":[TD([makeQuery(id+"F2.opExtrude","SWEPT_FACE",FACE,{"disambiguationData":[OSD([subQ5])]})])],"derivedFrom":makeQuery(id+"F3.boolean.opBoolean","COPY",FACE,{"derivedFrom":makeQuery(id+"F3.opExtrude","CAP_FACE",FACE,{"disambiguationData":[OSD([subQ5,subQ1,subQ6,subQ7,subQ4,subQ3,subQ2,subQ0])],"isStart":false})})}),makeQuery(id+"F8.opExtrude","SWEPT_FACE",FACE,{"disambiguationData":[OSD([sQuery(id+"F7.wireOp",EDGE,"E67")])]})]});}
            var Q5;
            Q5=makeQuery(id+"F8.boolean.opBoolean","INTERSECT",EDGE,{"disambiguationData":[OD(0.0)],"derivedFrom":[makeQuery(id+"F5.opExtrude","SWEPT_FACE",FACE,{"disambiguationData":[OSD([sQuery(id+"F4.wireOp",EDGE,"E30")])]}),makeQuery(id+"F8.opExtrude","SWEPT_FACE",FACE,{"disambiguationData":[OSD([sQuery(id+"F7.wireOp",EDGE,"E67")])]})]});
            fillet(context, id + "F14", {"entities" : qUnion([Q0, Q1, Q2, Q3, Q4, Q5]), "radius" : 3 * mm, "tangentPropagation" : true, "allowEdgeOverflow" : false});
        }
        {
            var Q0;
            Q0=makeQuery(id+"F1.opExtrude","CAP_EDGE",EDGE,{"disambiguationData":[OSD([sQuery(id+"F0.wireOp",EDGE,"E1.bottom")])],"isStart":false});
            fillet(context, id + "F15", {"entities" : qUnion([Q0]), "radius" : 2 * mm, "tangentPropagation" : true, "allowEdgeOverflow" : false});
        }
        {
            var Q0;
            Q0=qCreatedBy(makeId("Top.planeOp"),FACE);
            var sketch = newSketch(context, id + "F16", { "sketchPlane" : qUnion([Q0])});
            skCircle(sketch, "E79", {"center": v(0, 120) * mm, "radius": 6 * mm});
            skLineSegment(sketch, "E80", {"start": v(-33, 90) * mm, "end": v(-15, 108) * mm});
            skLineSegment(sketch, "E81", {"start": v(-15, 108) * mm, "end": v(-15, 120) * mm});
            skArc(sketch, "E82", {"start": v(15, 120) * mm, "mid": v(0, 135) * mm, "end": v(-15, 120) * mm});
            skLineSegment(sketch, "E83", {"start": v(0, 120) * mm, "end": v(0, 74.24) * mm, "construction": true});
            skLineSegment(sketch, "E84", {"start": v(15, 120) * mm, "end": v(15, 108) * mm});
            skLineSegment(sketch, "E85", {"start": v(15, 108) * mm, "end": v(33, 90) * mm});
            skCircle(sketch, "E86.MirrorC", {"center": v(0, -120) * mm, "radius": 6 * mm});
            skLineSegment(sketch, "E87.MirrorCS", {"start": v(15, -120) * mm, "end": v(15, -108) * mm});
            skLineSegment(sketch, "E88.MirrorCS", {"start": v(-15, -108) * mm, "end": v(-15, -120) * mm});
            skArc(sketch, "E89.MirrorCS", {"start": v(15, -120) * mm, "mid": v(0, -135) * mm, "end": v(-15, -120) * mm});
            skLineSegment(sketch, "E90.MirrorCS", {"start": v(-33, -90) * mm, "end": v(-15, -108) * mm});
            skLineSegment(sketch, "E91.MirrorCS", {"start": v(15, -108) * mm, "end": v(33, -90) * mm});
            skLineSegment(sketch, "E92.MirrorCS", {"start": v(0, -120) * mm, "end": v(0, -74.24) * mm, "construction": true});
            skLineSegment(sketch, "E93", {"start": v(-33, 90) * mm, "end": v(33, 90) * mm});
            skLineSegment(sketch, "E94.MirrorCS", {"start": v(-33, -90) * mm, "end": v(33, -90) * mm});
            skSolve(sketch);
        }
        {
            var Q0;
            Q0 = qSketchRegion(id + "F16", true);
            var Q1;
            Q1=makeQuery(id+"F2.opExtrude","CAP_FACE",FACE,{"disambiguationData":[OSD([sQuery(id+"F0.wireOp",EDGE,"E12"),sQuery(id+"F0.wireOp",EDGE,"E13"),sQuery(id+"F0.wireOp",EDGE,"E14"),sQuery(id+"F0.wireOp",EDGE,"E15"),sQuery(id+"F0.wireOp",EDGE,"E17.filletArc"),sQuery(id+"F0.wireOp",EDGE,"E18.filletArc"),sQuery(id+"F0.wireOp",EDGE,"E19.filletArc"),sQuery(id+"F0.wireOp",EDGE,"E20.filletArc"),sQuery(id+"F0.wireOp",EDGE,"E25.0"),sQuery(id+"F0.wireOp",EDGE,"E25.1"),sQuery(id+"F0.wireOp",EDGE,"E25.2"),sQuery(id+"F0.wireOp",EDGE,"E25.3"),sQuery(id+"F0.wireOp",EDGE,"E25.4"),sQuery(id+"F0.wireOp",EDGE,"E25.5"),sQuery(id+"F0.wireOp",EDGE,"E25.6"),sQuery(id+"F0.wireOp",EDGE,"E25.7")])],"isStart":false});
            extrude(context, id + "F17", {"entities" : qUnion([Q0]), "endBound" : BoundingType.UP_TO_SURFACE, "endBoundEntityFace" : qUnion([Q1]), "depth" : 25 * mm});
        }
    });
